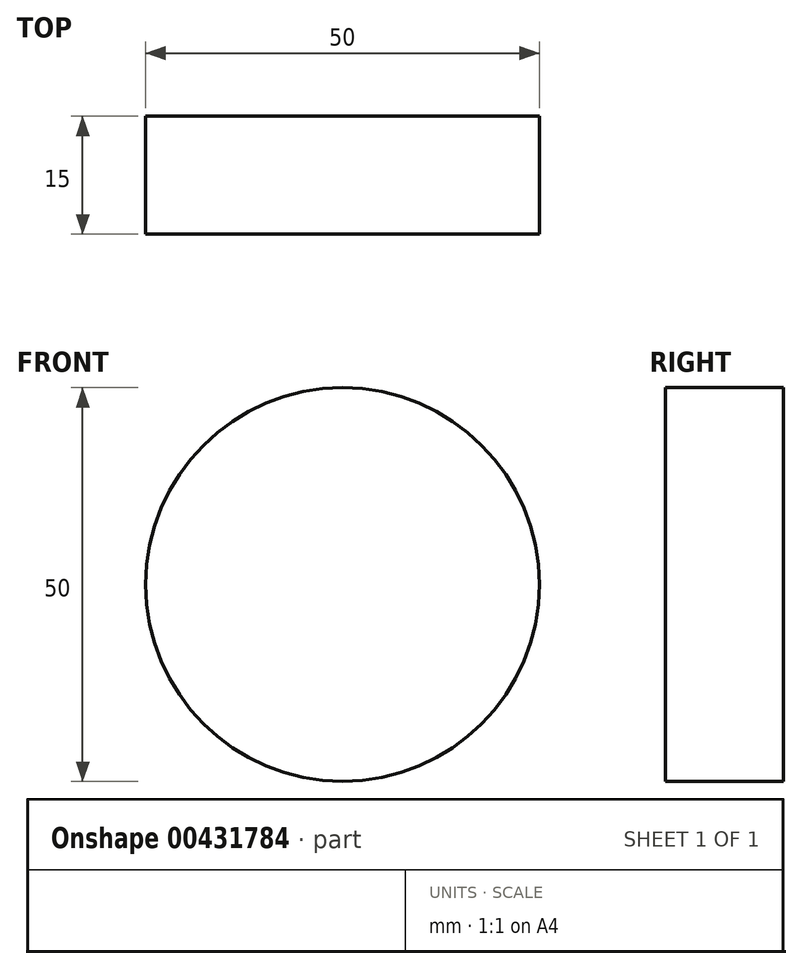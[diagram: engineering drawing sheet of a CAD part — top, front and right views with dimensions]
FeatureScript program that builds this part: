
annotation { "Feature Type Name" : "Feature", "Feature Type Description" : "" }
export const myFeature = defineFeature(function(context is Context, id is Id, definition is map)
    precondition{}
    {
        {
            var Q0;
            Q0=qCreatedBy(makeId("Front.planeOp"),FACE);
            var sketch = newSketch(context, id + "F0", { "sketchPlane" : qUnion([Q0])});
            skLineSegment(sketch, "E0", {"start": v(0, 0) * mm, "end": v(40.52, 0) * mm, "construction": true});
            skLineSegment(sketch, "E1.0", {"start": v(0, -25) * mm, "end": v(40.52, -25) * mm, "construction": true});
            skLineSegment(sketch, "E2", {"start": v(0, 0) * mm, "end": v(0, -25) * mm, "construction": true});
            skCircle(sketch, "E3", {"center": v(0, 0) * mm, "radius": 25 * mm});
            skSolve(sketch);
        }
        {
            var Q0;
            Q0=makeQuery(id+"F0.imprint","IMPRINT",FACE,{"disambiguationData":[TD([[makeQuery(id+"F0.imprint","IMPRINT",EDGE,{"derivedFrom":sQuery(id+"F0.wireOp",EDGE,"E3")}),1.0]])]});
            extrude(context, id + "F1", {"entities" : qUnion([Q0]), "depth" : 15 * mm});
        }
    });
